# Revit family: Suszarka_do_rak_PASSAT H
name_source: partatom
category: Wyposażenie elektryczne
units: mm (PartAtom-declared; Revit-internal decimal feet)

## family parameters
Konfiguracja rozdzielnicy = Dwie kolumny, obwody w poprzek
Obiekt nadrzędny = Ściana
Punkt obliczania pomieszczeń = Nie
Tnij formami wycięć po wczytaniu = Nie
Typ części = Rozdzielnica
Współdzielony = Nie
Wymiar okrągłego złącza = Użyj średnicy
Zawsze pionowo = Tak

## types (1)
- Type 1
    Depth / Glebokosc = 150 mm
    Height / Wysokosc = 173 mm
    Komentarze do typu = Suszarka do rąk 1350 W PASSAT H
    Manufacturer code / Kod producenta = 5901764293989
    Material finish / Wykonczenie = Stal nierdzewna 304 szczotkowana
    Moc w watach = 1350
    Model = PASSAT H
    Opis = Suszarka do rąk 1350 Passat H to energooszczędne urządzenie, wykonane ze stali nierdzewnej szczotkowanej. Włącza się samoczynnie po wsunięciu dłoni w pole działania czujnika. Dzięki swej niezawodności, cichej pracy oraz ciekawemu wyglądowi idealnie pasuje do różnorodnych łazienek publicznych o średnim i dużym natężeniu ruchu. To wydajna i wandaloodporna suszarka do rąk, która posiada specjalną dyszę, pozwalającą skrócić czas suszenia rąk do minimum. Passat jest świetną alternatywą dla ręczników papierowych.
    Producent = FANECO.com
    Product code / Kod produktu = D1350SCBH
    URL = https://faneco.com
    Weight / Waga = 3 kg
    Width / Szerokosc = 255 mm  [stored 0.836614 ft]

note: [stored X ft] marks values corroborated as IEEE doubles in the binary element streams (Revit-internal decimal feet)

## geometry (parser evidence)
native form markers: Blend x8, Sweep x4
no freeform markers — native parametric forms only
